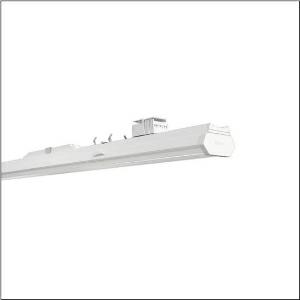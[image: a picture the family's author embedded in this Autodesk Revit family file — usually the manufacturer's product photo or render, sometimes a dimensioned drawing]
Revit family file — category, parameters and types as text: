
# Revit family: licross_r__11_protected_extreme_ho_51tp12dn4fxme_36ff
name_source: partatom
category: Lighting Fixtures
units: mm (PartAtom-declared; Revit-internal decimal feet)

## family parameters
Cut with Voids When Loaded = No
Host = Face
Light Source = No
Part Type = Normal
Room Calculation Point = No
Round Connector Dimension = Use Diameter
Shared = No

## types (1)
- --- (1 x LED, 15270 lm, 87.3 W, 4000K)
    Apparent Load = 87 VA
    CIE Flux Codes = 70 91 97 98 100
    Color Rendering = 80
    Color Temperature = 4000K
    Default Elevation = 1800 mm
    Description = Licross® 11 Protected extreme HO, luminaire insert, of sheet steel, galvanised, coil coated, white, length: 1.500mm, width: 90mm, height: 101mm, LED rated luminous flux: 15.270lm, light colour: 840, control gear: DALI 2, with plug, 5-pole, with phase selection, mains connection: 220..240V, AC, 50/60Hz, rated input power: 87W, halogen-free wiring, primary optical cover: cover, of PMMA, light emission: direct distribution, primary light characteristic: symmetric, protection rating (complete): IP64, insulation class (complete): insulation class I (protective earthing), certification: CE, ENEC, VDE, UKCA, protection symbol: D if used in an environment with conductive dust loads with corresponding accessories, impact resistance: IK06, permissible ambient temperature for indoor applications: -40..+40°C, corresponds to IFS (International Featured Standards) requirements for safety and quality in the food industry, reducing of maximum allowable ambient temperature of 5°C with ceiling mounting, LABS conformity tested according to VDMA 24364:2018-05, packaging unit: 1 piece
    Height = 92 mm
    Lamp = 1 x LED
    Lamp Light Flux = 15270 lm
    Lamp Power = 87.3 W
    Lamp count = 1
    Length = 1500 mm
    Luminous efficacy = 175 lm/W
    Manufacturer = Siteco
    ModVariant = No
    Model = 51TP12DN4FXME
    Mounting Place = Ceiling
    Mounting Type = Pendant
    Number of Poles = 1
    OnlyDefault = Yes
    Power Factor = 1
    Product Name = Licross® 11 Protected extreme HO
    Product group = luminaire insert
    ProductGroupID = 902
    Protection Class = Protection class I
    Protection Degree = IP 64
    RLX_Detail_Level = 1
    RLX_Emergency_Light_Flux = 0 lm
    RLX_Emergency_Type = 0
    RLX_Emergency_Type_DB = No
    RlxData = <blob elided: 24409 chars, md5=13857af5>
    Socket = socket
    Standby Power = 0 W
    System Light Flux = 15270 lm
    System Power = 87 W
    Type Comments = factory setting: luminous flux: 100 % | dim-lin: 254 | 589 mA
    Type Image = l_1256148.jpg
    URL = http://relux.com
    VarID = @adj_082700
    Voltage = 0 V
    Weight = 0.00 kg
    Width = 88 mm

## geometry (parser evidence)
native form markers: Blend x4, Sweep x11
no freeform markers — native parametric forms only
